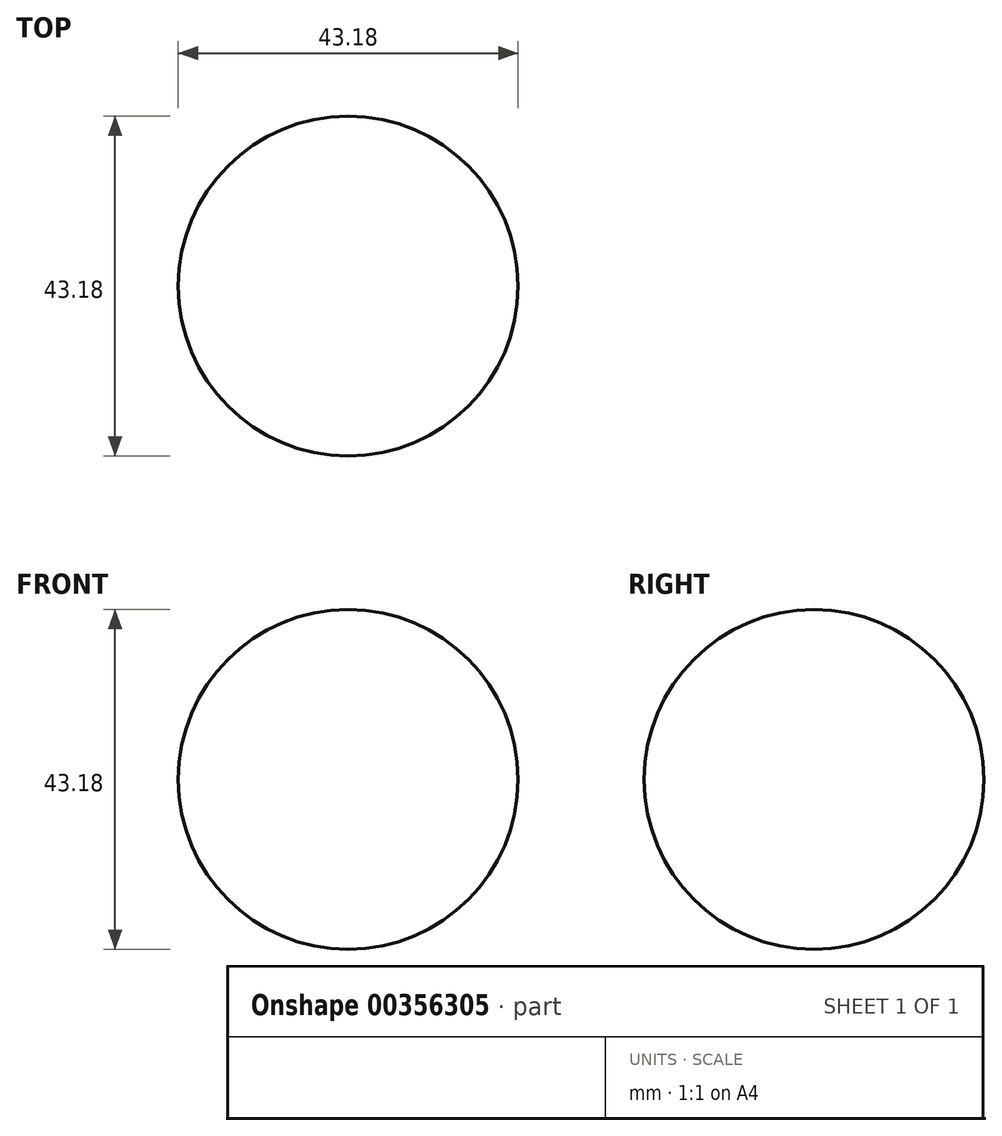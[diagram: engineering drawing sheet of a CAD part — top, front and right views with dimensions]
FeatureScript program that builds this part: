
annotation { "Feature Type Name" : "Feature", "Feature Type Description" : "" }
export const myFeature = defineFeature(function(context is Context, id is Id, definition is map)
    precondition{}
    {
        {
            var Q0;
            Q0=qCreatedBy(makeId("Front.planeOp"),FACE);
            var sketch = newSketch(context, id + "F0", { "sketchPlane" : qUnion([Q0])});
            skArc(sketch, "E0", {"start": v(0, 20.1) * mm, "mid": v(-21.59, -1.49) * mm, "end": v(0, -23.08) * mm});
            skLineSegment(sketch, "E1", {"start": v(0, 20.1) * mm, "end": v(0, -23.08) * mm});
            skSolve(sketch);
        }
        {
            var Q0;
            Q0=qSketchRegion(id+"F0",true);
            var Q1;
            Q1=sQuery(id+"F0.wireOp",EDGE,"E1");
            revolve(context, id + "F1", {"entities" : qUnion([Q0]), "axis" : qUnion([Q1]), "revolveType" : RevolveType.FULL});
        }
    });
